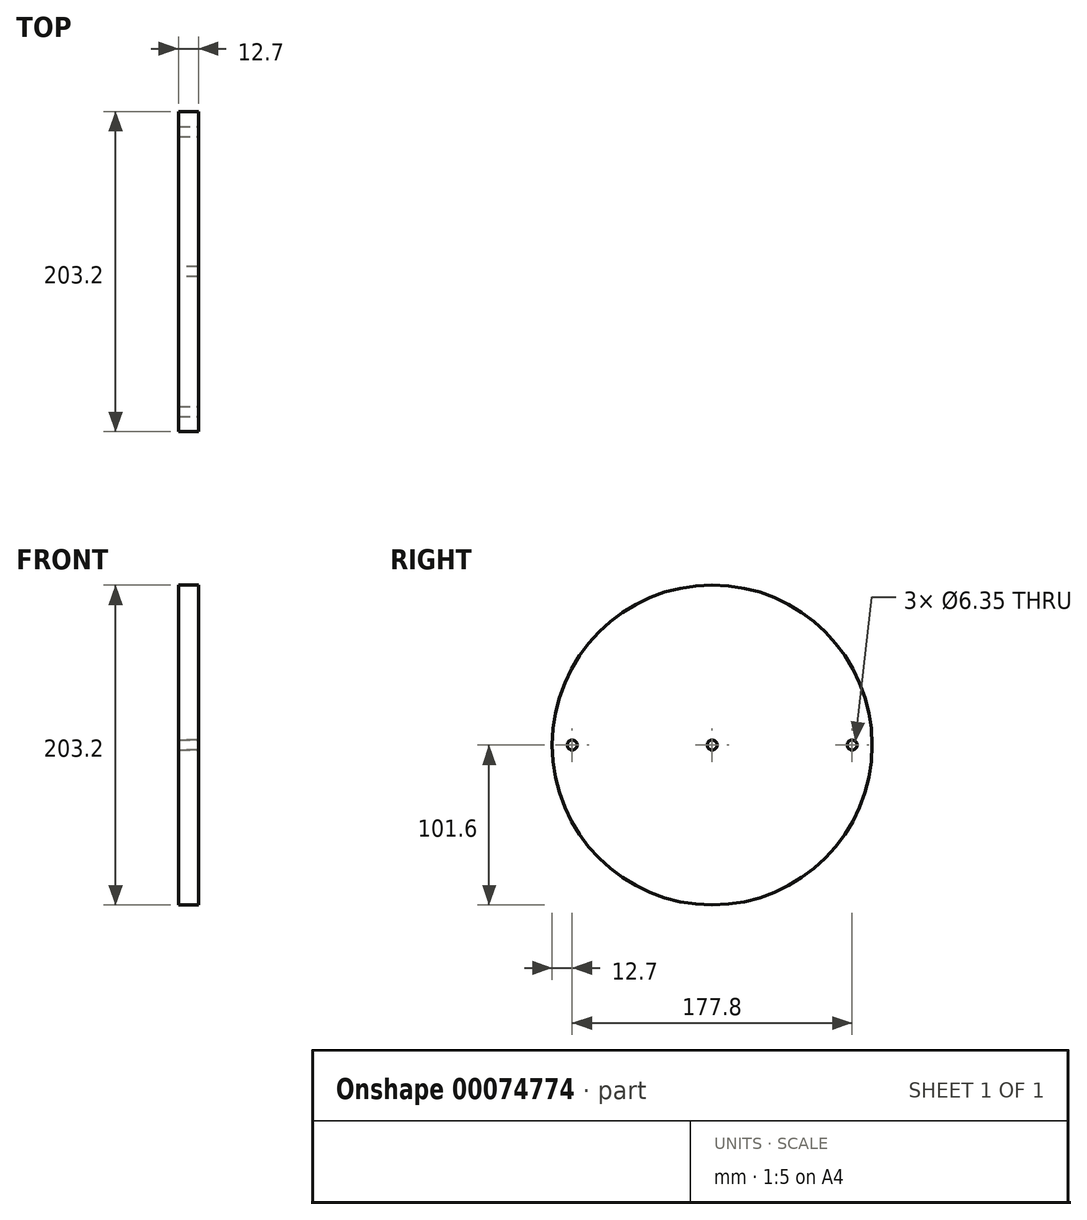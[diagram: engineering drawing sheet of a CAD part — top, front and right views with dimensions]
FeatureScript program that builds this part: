
annotation { "Feature Type Name" : "Feature", "Feature Type Description" : "" }
export const myFeature = defineFeature(function(context is Context, id is Id, definition is map)
    precondition{}
    {
        {
            var Q0;
            Q0=qCreatedBy(makeId("Right.planeOp"),FACE);
            var sketch = newSketch(context, id + "F0", { "sketchPlane" : qUnion([Q0])});
            skCircle(sketch, "E0", {"center": v(0, 0) * mm, "radius": 101.6 * mm});
            skSolve(sketch);
        }
        {
            var Q0;
            Q0=makeQuery(id+"F0.imprint","IMPRINT",FACE,{"disambiguationData":[TD([[makeQuery(id+"F0.imprint","IMPRINT",EDGE,{"derivedFrom":sQuery(id+"F0.wireOp",EDGE,"E0")}),1.0]])]});
            var sketch = newSketch(context, id + "F1", { "sketchPlane" : qUnion([Q0])});
            skPoint(sketch, "E1", {"position": v(0, 0) * mm});
            skSolve(sketch);
        }
        {
            var Q0;
            Q0=makeQuery(id+"F0.imprint","IMPRINT",FACE,{"disambiguationData":[TD([[makeQuery(id+"F0.imprint","IMPRINT",EDGE,{"derivedFrom":sQuery(id+"F0.wireOp",EDGE,"E0")}),1.0]])]});
            extrude(context, id + "F2", {"entities" : qUnion([Q0]), "depth" : 12.7 * mm});
        }
        {
            var Q0;
            Q0=sQuery(id+"F1.wireOp",VERTEX,"E1");
            var Q1;
            Q1=makeQuery(id+"F2.opExtrude","SWEPT_BODY",BODY,{"disambiguationData":[OSD([sQuery(id+"F0.wireOp",EDGE,"E0")])]});
            hole(context, id + "F3", {"style" : HoleStyle.SIMPLE, "holeDiameter" : 6.35 * mm, "endStyle" : HoleEndStyle.THROUGH, "oppositeDirection" : true, "locations" : qUnion([Q0]), "scope" : qUnion([Q1])});
        }
        {
            var Q0;
            Q0=makeQuery(id+"F2.opExtrude","CAP_FACE",FACE,{"disambiguationData":[OSD([sQuery(id+"F0.wireOp",EDGE,"E0")])],"isStart":false});
            var sketch = newSketch(context, id + "F4", { "sketchPlane" : qUnion([Q0])});
            skPoint(sketch, "E2", {"position": v(88.9, 0) * mm});
            skSolve(sketch);
        }
        {
            var Q0;
            Q0=sQuery(id+"F4.wireOp",VERTEX,"E2");
            var Q1;
            Q1=makeQuery(id+"F2.opExtrude","SWEPT_BODY",BODY,{"disambiguationData":[OSD([sQuery(id+"F0.wireOp",EDGE,"E0")])]});
            hole(context, id + "F5", {"style" : HoleStyle.SIMPLE, "holeDiameter" : 6.35 * mm, "endStyle" : HoleEndStyle.THROUGH, "locations" : qUnion([Q0]), "scope" : qUnion([Q1])});
        }
        {
            var Q0;
            Q0=makeQuery(id+"F2.opExtrude","CAP_FACE",FACE,{"disambiguationData":[OSD([sQuery(id+"F0.wireOp",EDGE,"E0")])],"isStart":false});
            var sketch = newSketch(context, id + "F6", { "sketchPlane" : qUnion([Q0])});
            skPoint(sketch, "E3", {"position": v(-88.9, 0) * mm});
            skSolve(sketch);
        }
        {
            var Q0;
            Q0=sQuery(id+"F6.wireOp",VERTEX,"E3");
            var Q1;
            Q1=makeQuery(id+"F2.opExtrude","SWEPT_BODY",BODY,{"disambiguationData":[OSD([sQuery(id+"F0.wireOp",EDGE,"E0")])]});
            hole(context, id + "F7", {"style" : HoleStyle.SIMPLE, "endStyle" : HoleEndStyle.THROUGH, "holeDiameter" : 6.35 * mm, "locations" : qUnion([Q0]), "scope" : qUnion([Q1]), "isTappedThrough" : true});
        }
    });
